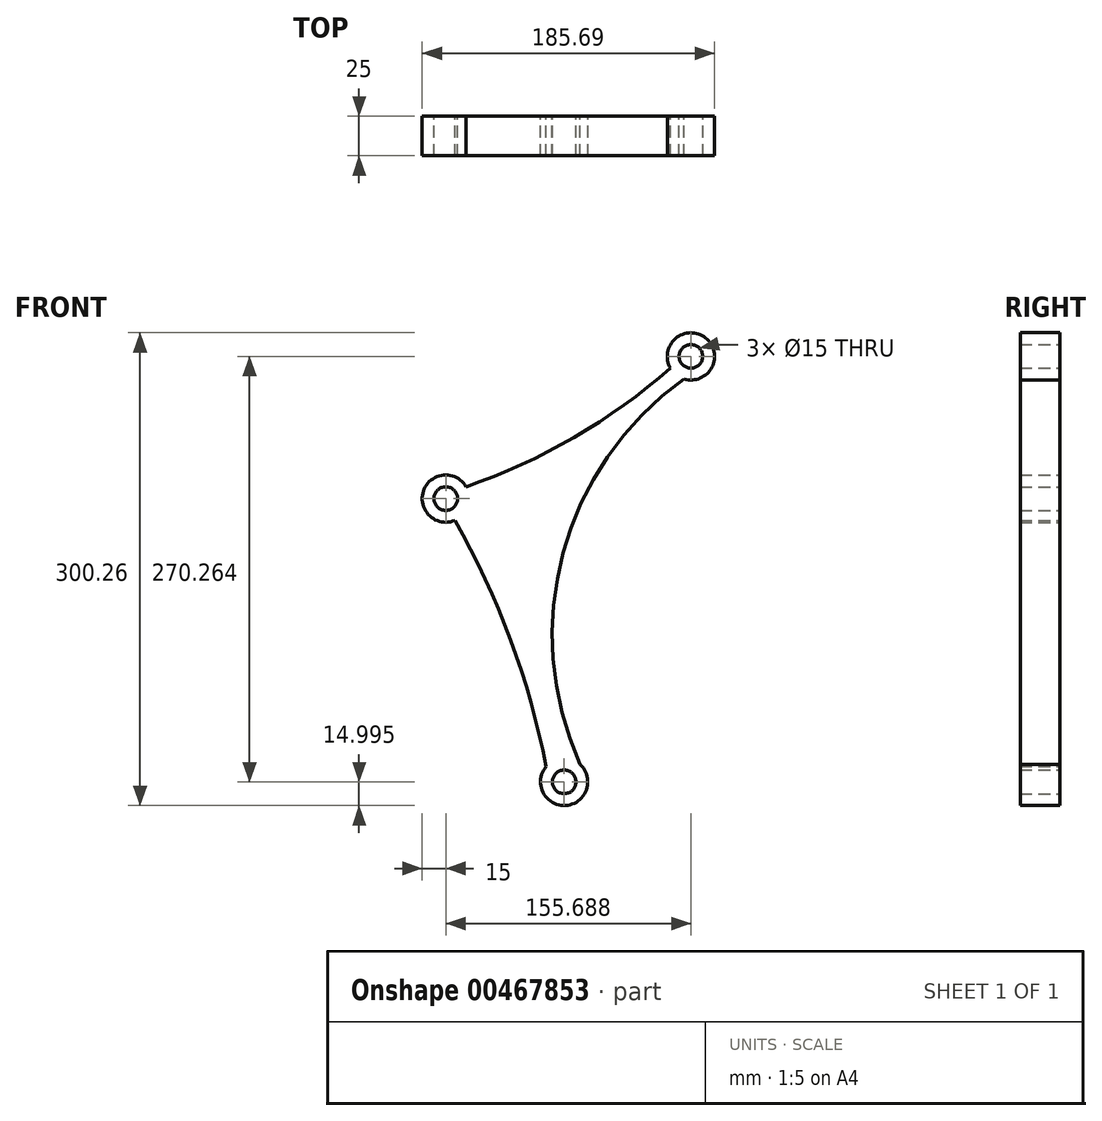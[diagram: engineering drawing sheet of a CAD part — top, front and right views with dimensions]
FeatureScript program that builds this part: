
annotation { "Feature Type Name" : "Feature", "Feature Type Description" : "" }
export const myFeature = defineFeature(function(context is Context, id is Id, definition is map)
    precondition{}
    {
        {
            var Q0;
            Q0=qCreatedBy(makeId("Front.planeOp"),FACE);
            var sketch = newSketch(context, id + "F0", { "sketchPlane" : qUnion([Q0])});
            skCircle(sketch, "E0", {"center": v(155.69, 90.34) * mm, "radius": 15 * mm});
            skCircle(sketch, "E1", {"center": v(0, 0) * mm, "radius": 15 * mm});
            skCircle(sketch, "E2", {"center": v(75.18, -179.92) * mm, "radius": 15 * mm});
            skLineSegment(sketch, "E3", {"start": v(0, 0) * mm, "end": v(155.69, 90.34) * mm, "construction": true});
            skLineSegment(sketch, "E4", {"start": v(0, 0) * mm, "end": v(75.18, -179.92) * mm, "construction": true});
            skLineSegment(sketch, "E5", {"start": v(155.69, 90.34) * mm, "end": v(75.18, -179.92) * mm, "construction": true});
            skCircle(sketch, "E6", {"center": v(0, 0) * mm, "radius": 7.5 * mm});
            skCircle(sketch, "E7", {"center": v(155.69, 90.34) * mm, "radius": 7.5 * mm});
            skCircle(sketch, "E8", {"center": v(75.18, -179.92) * mm, "radius": 7.5 * mm});
            skArc(sketch, "E9", {"start": v(12.97, 7.53) * mm, "mid": v(81.47, 38.93) * mm, "end": v(142.71, 82.81) * mm});
            skArc(sketch, "E10", {"start": v(63.79, -170.17) * mm, "mid": v(41.12, -89.65) * mm, "end": v(5.78, -13.84) * mm});
            skArc(sketch, "E11", {"start": v(151.4, 75.96) * mm, "mid": v(74.5, -34.63) * mm, "end": v(85.35, -168.9) * mm});
            skSolve(sketch);
        }
        {
            var Q0;
            Q0 = qSketchRegion(id + "F0", true);
            extrude(context, id + "F1", {"entities" : qUnion([Q0]), "depth" : 25 * mm});
        }
    });
